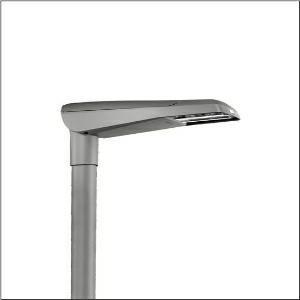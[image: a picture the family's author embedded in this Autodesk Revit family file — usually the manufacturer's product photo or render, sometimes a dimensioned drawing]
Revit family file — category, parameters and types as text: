
# Revit family: streetlight_sl_11_iq_micro___st1_2a_5xc1ac1g08de_fbfe
name_source: partatom
category: Lighting Fixtures
units: mm (PartAtom-declared; Revit-internal decimal feet)

## family parameters
Cut with Voids When Loaded = No
Host = Face
Light Source = No
Part Type = Normal
Room Calculation Point = No
Round Connector Dimension = Use Diameter
Shared = No

## types (1)
- --- (1 x LED, 3860 lm, 27.4 W, 4000K)
    Apparent Load = 27 VA
    CIE Flux Codes = 33 71 96 100 100
    Color Rendering = 70
    Color Temperature = 4000K
    Default Elevation = 1800 mm
    Description = Streetlight SL 11 iQ micro, mast luminaire, primary light control with 3 zone facetted reflector, of plastic, silver coated, highly specular, primary optical cover: cover, of PMMA, transparent, light distribution: ST1.2a, light emission: direct distribution, primary light characteristic: asymmetric, installation type: post-top, side-entry, lamps: LED, High Power LED, rated values: 3.620lm | 27,7W | 130,7lm/W (begin service life); end service life: 3.620lm | 28,1W; at 50% lumin. flux: 1.810lm | 13,4W | 135,1lm/W, colour temperature: 2200/2700/3000/4000K, colour rendering: CRI > 70, light colour: 722/727/730/740, light setting 1 begin service life: 100% | 3.620lm | 27,7W | 130,7lm/W | 3.000K, light setting 1 end service life: 28,1W, further light settings possible, control: pre-setting: linear dimming characteristic, Street-Remote, Auto-Match, Temp-Guard, Lumen-Switch, Night-Set, Smart-Wire, Light-Fading, Desk-Remote (wireless, voltage-free reading and setting of iQ features in the workshop via application-optimized NFC function/RFID function), optimised constant luminous flux control (CLO 2.0), with cable H07RN-F 5x 1.5mm², mains connection: 220..240V, AC, 50/60Hz, connection cable pre-assembled, cable length: 6,5m, luminaire housing, of diecast aluminium, powder-coated, Siteco® metallic grey (DB 702S), please order mast flange separately, inclination adjustable without tools: 0°, 5°, 10°, 15° (post-top) | 0°, -5°, -10°, -15° (side-entry), sealing non-destructively replaceable, multi-level sealing system, length: 600mm, width: 174mm, height: 116mm, mast flange for spigot size: 42mm (side-entry): 5XC10008XM4, 60/48mm (side-entry/post-top): 5XC10108XM2, 76/60mm (side-entry/post-top): 5XC10108XM1, equipment: Power, protection rating (complete): IP66, insulation class (complete): insulation class II (safety insulation), certification: CE, ENEC, ENEC+, VDE, impact resistance: IK10, permissible operating ambient temperature for outdoor applications: -25..+50°C, standard-compliant lighting for roads and squares, Environmental Product Declaration (EPD) tested and certified by an independent institute, packaging unit: 1 piece

Light Distribution: ST1.2a
    Height = 116 mm
    Lamp = 1 x LED
    Lamp Light Flux = 3860 lm
    Lamp Power = 27.4 W
    Lamp count = 1
    Length = 600 mm
    Luminous efficacy = 141 lm/W
    Manufacturer = Siteco
    ModVariant = No
    Model = 5XC1AC1G08DE
    Number of Poles = 1
    OnlyDefault = Yes
    Power Factor = 1
    Product Name = Streetlight SL 11 iQ micro | ST1.2a
    Product group = mast luminaire | pylon top
    ProductGroupID = 6100
    Protection Class = Protection class II
    Protection Degree = IP 66
    RLX_Detail_Level = 1
    RLX_Emergency_Light_Flux = 0 lm
    RLX_Emergency_Type = 0
    RLX_Emergency_Type_DB = No
    RlxData = <blob elided: 59909 chars, md5=7dc9fa65>
    Socket = socket
    Standby Power = 0 W
    System Light Flux = 3860 lm
    System Power = 27 W
    Type Comments = individual setting: luminous flux: 100 % | dim-lin: 254 | 726 mA
    Type Image = l_1006566.jpg
    URL = http://relux.com
    VarID = @adj_060723
    Voltage = 0 V
    Weight = 0.00 kg
    Width = 174 mm

## geometry (parser evidence)
native form markers: Blend x4, Sweep x13
no freeform markers — native parametric forms only
